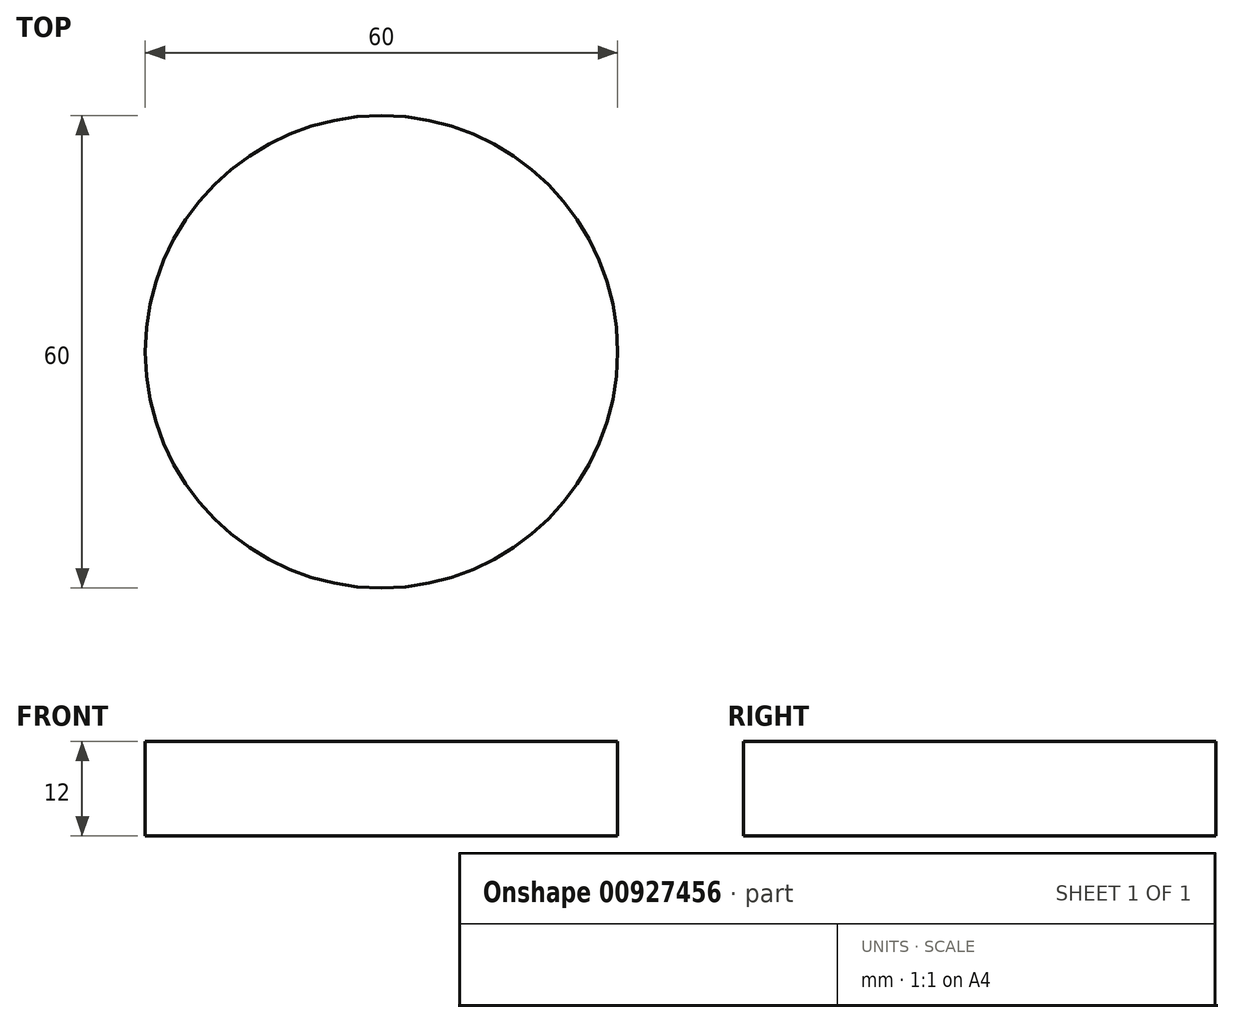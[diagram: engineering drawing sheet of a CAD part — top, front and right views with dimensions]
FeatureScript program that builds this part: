
annotation { "Feature Type Name" : "Feature", "Feature Type Description" : "" }
export const myFeature = defineFeature(function(context is Context, id is Id, definition is map)
    precondition{}
    {
        {
            var Q0;
            Q0=qCreatedBy(makeId("Top.planeOp"),FACE);
            var sketch = newSketch(context, id + "F0", { "sketchPlane" : qUnion([Q0])});
            skCircle(sketch, "E0", {"center": v(0, 0) * mm, "radius": 30 * mm});
            skSolve(sketch);
        }
        {
            var Q0;
            Q0=makeQuery(id+"F0.imprint","IMPRINT",FACE,{"disambiguationData":[TD([[makeQuery(id+"F0.imprint","IMPRINT",EDGE,{"derivedFrom":sQuery(id+"F0.wireOp",EDGE,"E0")}),1.0]])]});
            extrude(context, id + "F1", {"entities" : qUnion([Q0]), "depth" : 12 * mm, "offsetDistance" : 25 * mm});
        }
    });
